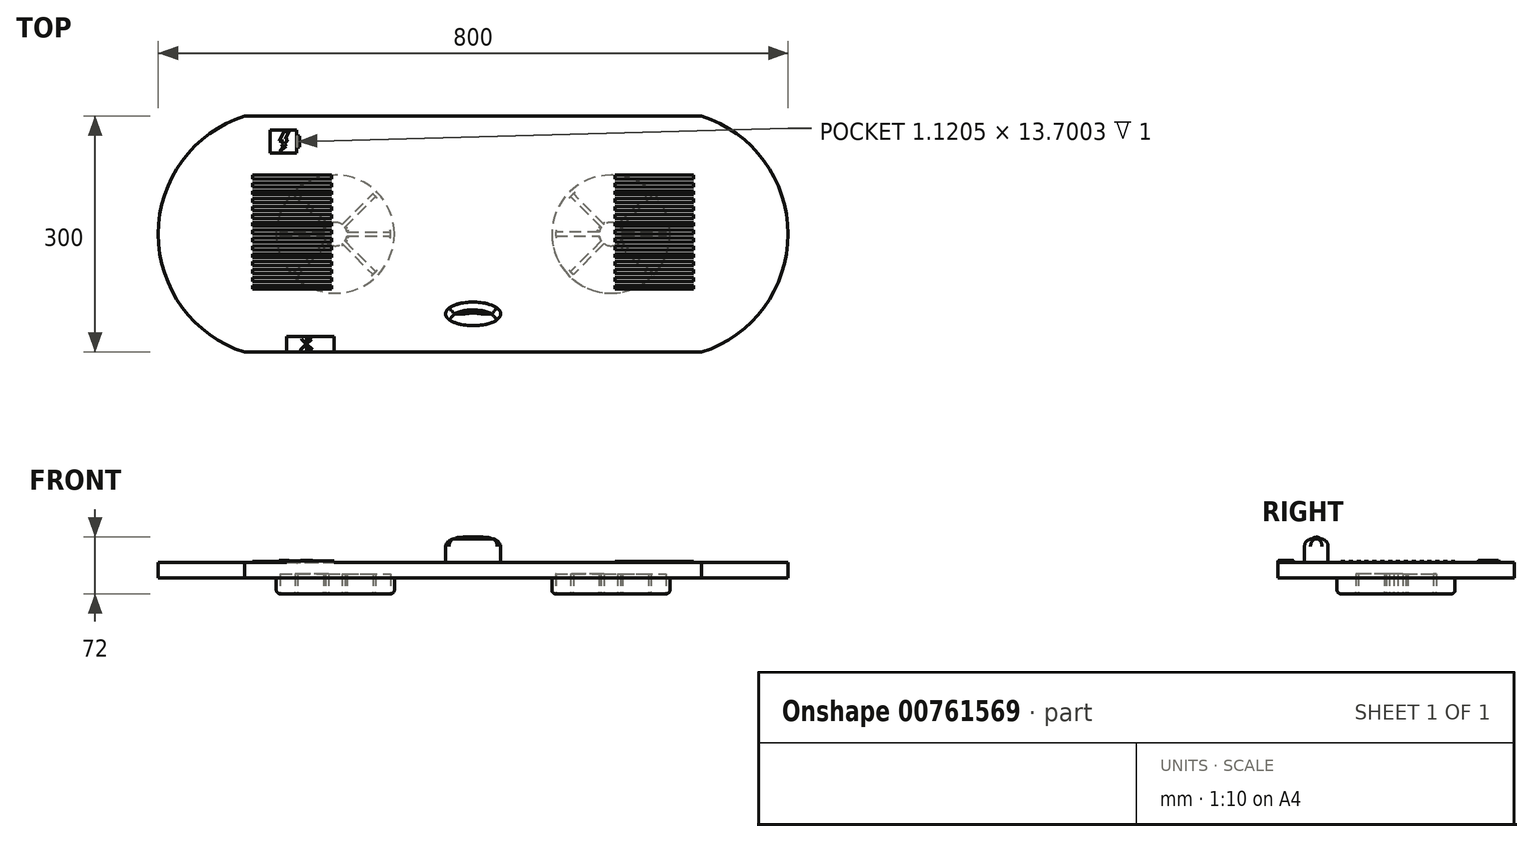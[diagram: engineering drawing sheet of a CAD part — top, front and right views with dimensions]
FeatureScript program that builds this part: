
annotation { "Feature Type Name" : "Feature", "Feature Type Description" : "" }
export const myFeature = defineFeature(function(context is Context, id is Id, definition is map)
    precondition{}
    {
        {
            var Q0;
            Q0=qCreatedBy(makeId("Top.planeOp"),FACE);
            var sketch = newSketch(context, id + "F0", { "sketchPlane" : qUnion([Q0])});
            skLineSegment(sketch, "E0.bottom", {"start": v(400, 150) * mm, "end": v(-400, 150) * mm});
            skLineSegment(sketch, "E0.top", {"start": v(400, -150) * mm, "end": v(-400, -150) * mm});
            skLineSegment(sketch, "E0.left", {"start": v(400, 150) * mm, "end": v(400, -150) * mm});
            skLineSegment(sketch, "E0.right", {"start": v(-400, 150) * mm, "end": v(-400, -150) * mm});
            skPoint(sketch, "E0.middle", {"position": v(0, 0) * mm});
            skArc(sketch, "E1", {"start": v(-290, 150) * mm, "mid": v(-400, 0) * mm, "end": v(-290, -150) * mm});
            skArc(sketch, "E2", {"start": v(290, -150) * mm, "mid": v(400, 0) * mm, "end": v(290, 150) * mm});
            skSolve(sketch);
        }
        {
            var Q0;
            {var subQ0=sQuery(id+"F0.wireOp",EDGE,"E1");var subQ1=sQuery(id+"F0.wireOp",EDGE,"E0.bottom");var subQ2=makeQuery(id+"F0.imprint","INTERSECT",VERTEX,{"derivedFrom":[subQ1,subQ0]});Q0=makeQuery(id+"F0.imprint","IMPRINT",FACE,{"disambiguationData":[TD([[makeQuery(id+"F0.imprint","IMPRINT",EDGE,{"disambiguationData":[TD([[subQ2,1.0]])],"derivedFrom":subQ1}),1.0]])]});}
            extrude(context, id + "F1", {"entities" : qUnion([Q0]), "depth" : 20 * mm, "offsetDistance" : 25 * mm});
        }
        {
            var Q0;
            Q0=makeQuery(id+"F1.opExtrude","CAP_FACE",FACE,{"disambiguationData":[OSD([sQuery(id+"F0.wireOp",EDGE,"E0.bottom"),sQuery(id+"F0.wireOp",EDGE,"E0.top"),sQuery(id+"F0.wireOp",EDGE,"E1"),sQuery(id+"F0.wireOp",EDGE,"E2")])],"isStart":true});
            var sketch = newSketch(context, id + "F2", { "sketchPlane" : qUnion([Q0])});
            skCircle(sketch, "E3", {"center": v(-175, 0) * mm, "radius": 75 * mm});
            skCircle(sketch, "E4", {"center": v(175, 0) * mm, "radius": 75 * mm});
            skSolve(sketch);
        }
        {
            var Q0;
            Q0=makeQuery(id+"F2.imprint","IMPRINT",FACE,{"disambiguationData":[TD([[makeQuery(id+"F2.imprint","IMPRINT",EDGE,{"derivedFrom":sQuery(id+"F2.wireOp",EDGE,"E3")}),1.0]])]});
            var Q1;
            Q1=makeQuery(id+"F2.imprint","IMPRINT",FACE,{"disambiguationData":[TD([[makeQuery(id+"F2.imprint","IMPRINT",EDGE,{"derivedFrom":sQuery(id+"F2.wireOp",EDGE,"E4")}),1.0]])]});
            extrude(context, id + "F3", {"entities" : qUnion([Q0, Q1]), "operationType" : NewBodyOperationType.ADD, "depth" : 20 * mm, "offsetDistance" : 25 * mm});
        }
        {
            var Q0;
            Q0=makeQuery(id+"F3.opExtrude","CAP_FACE",FACE,{"disambiguationData":[OSD([sQuery(id+"F2.wireOp",EDGE,"E3")])],"isStart":false});
            var Q1;
            Q1=makeQuery(id+"F3.opExtrude","CAP_FACE",FACE,{"disambiguationData":[OSD([sQuery(id+"F2.wireOp",EDGE,"E4")])],"isStart":false});
            fillet(context, id + "F4", {"entities" : qUnion([Q0, Q1]), "radius" : 5 * mm, "tangentPropagation" : true, "allowEdgeOverflow" : false});
        }
        {
            var Q0;
            Q0=makeQuery(id+"F1.opExtrude","CAP_FACE",FACE,{"disambiguationData":[OSD([sQuery(id+"F0.wireOp",EDGE,"E0.bottom"),sQuery(id+"F0.wireOp",EDGE,"E0.top"),sQuery(id+"F0.wireOp",EDGE,"E1"),sQuery(id+"F0.wireOp",EDGE,"E2")])],"isStart":false});
            var sketch = newSketch(context, id + "F5", { "sketchPlane" : qUnion([Q0])});
            skLineSegment(sketch, "E5.bottom", {"start": v(-236.75, -150) * mm, "end": v(-176.75, -150) * mm});
            skLineSegment(sketch, "E5.top", {"start": v(-236.75, -130) * mm, "end": v(-176.75, -130) * mm});
            skLineSegment(sketch, "E5.left", {"start": v(-236.75, -150) * mm, "end": v(-236.75, -130) * mm});
            skLineSegment(sketch, "E5.right", {"start": v(-176.75, -150) * mm, "end": v(-176.75, -130) * mm});
            skSolve(sketch);
        }
        {
            var Q0;
            Q0=makeQuery(id+"F5.imprint","IMPRINT",FACE,{"disambiguationData":[TD([[makeQuery(id+"F5.imprint","IMPRINT",EDGE,{"derivedFrom":sQuery(id+"F5.wireOp",EDGE,"E5.bottom")}),-1.0]])]});
            var sketch = newSketch(context, id + "F6", { "sketchPlane" : qUnion([Q0])});
            skLineSegment(sketch, "E6", {"start": v(-219.31, -146.88) * mm, "end": v(-218.82, -147.38) * mm});
            skLineSegment(sketch, "E7", {"start": v(-212.24, -139.81) * mm, "end": v(-218.05, -134) * mm});
            skLineSegment(sketch, "E8", {"start": v(-218.05, -134) * mm, "end": v(-217.56, -133.5) * mm});
            skLineSegment(sketch, "E9", {"start": v(-211.74, -139.32) * mm, "end": v(-211.74, -130.32) * mm});
            skLineSegment(sketch, "E10", {"start": v(-211.74, -130.32) * mm, "end": v(-205.43, -134) * mm});
            skLineSegment(sketch, "E11", {"start": v(-211.74, -140.3) * mm, "end": v(-211.74, -149.3) * mm});
            skLineSegment(sketch, "E12", {"start": v(-212.24, -139.81) * mm, "end": v(-219.31, -146.88) * mm});
            skLineSegment(sketch, "E13", {"start": v(-204.18, -146.88) * mm, "end": v(-211.74, -149.3) * mm});
            skLineSegment(sketch, "E14", {"start": v(-211.74, -140.3) * mm, "end": v(-218.82, -147.38) * mm});
            skLineSegment(sketch, "E15", {"start": v(-211.25, -139.81) * mm, "end": v(-210.45, -139.02) * mm});
            skLineSegment(sketch, "E16", {"start": v(-210.45, -139.02) * mm, "end": v(-205.43, -134) * mm});
            skLineSegment(sketch, "E17", {"start": v(-217.56, -133.5) * mm, "end": v(-211.74, -139.32) * mm});
            skLineSegment(sketch, "E18", {"start": v(-204.18, -146.88) * mm, "end": v(-211.25, -139.81) * mm});
            skLineSegment(sketch, "E19", {"start": v(-211.25, -131.3) * mm, "end": v(-211.25, -138.81) * mm});
            skLineSegment(sketch, "E20", {"start": v(-211.25, -131.3) * mm, "end": v(-207.16, -133.69) * mm});
            skLineSegment(sketch, "E21", {"start": v(-207.16, -133.69) * mm, "end": v(-206.93, -133.82) * mm});
            skLineSegment(sketch, "E22", {"start": v(-206.93, -133.82) * mm, "end": v(-211.25, -138.81) * mm});
            skLineSegment(sketch, "E23", {"start": v(-211.25, -140.95) * mm, "end": v(-211.25, -148.29) * mm});
            skLineSegment(sketch, "E24", {"start": v(-211.25, -148.29) * mm, "end": v(-206.47, -146.82) * mm});
            skLineSegment(sketch, "E25", {"start": v(-206.47, -146.82) * mm, "end": v(-211.25, -140.95) * mm});
            skSolve(sketch);
        }
        {
            var Q0;
            Q0=makeQuery(id+"F6.imprint","IMPRINT",FACE,{"disambiguationData":[TD([[makeQuery(id+"F6.imprint","IMPRINT",EDGE,{"derivedFrom":sQuery(id+"F6.wireOp",EDGE,"E6")}),1.0]])]});
            var Q1;
            Q1 = qSketchRegion(id + "F8", true);
            var Q2;
            Q2 = qSketchRegion(id + "F5", true);
            extrude(context, id + "F7", {"entities" : qUnion([Q0, Q1, Q2]), "operationType" : NewBodyOperationType.ADD, "depth" : 2 * mm, "offsetDistance" : 25 * mm});
        }
        {
            var Q0;
            Q0=makeQuery(id+"F3.opExtrude","CAP_FACE",FACE,{"disambiguationData":[OSD([sQuery(id+"F2.wireOp",EDGE,"E3")])],"isStart":false});
            var sketch = newSketch(context, id + "F8", { "sketchPlane" : qUnion([Q0])});
            skCircle(sketch, "E26", {"center": v(-175, 0) * mm, "radius": 15 * mm});
            skLineSegment(sketch, "E27", {"start": v(-177.5, 14.8) * mm, "end": v(-177.5, 70) * mm});
            skLineSegment(sketch, "E28", {"start": v(-172.5, 14.8) * mm, "end": v(-172.5, 69.96) * mm});
            skLineSegment(sketch, "E29", {"start": v(-177.5, -14.8) * mm, "end": v(-177.5, -69.96) * mm});
            skLineSegment(sketch, "E30", {"start": v(-172.5, -14.8) * mm, "end": v(-172.5, -69.96) * mm});
            skLineSegment(sketch, "E31", {"start": v(-190, 2.5) * mm, "end": v(-189.8, 2.5) * mm});
            skLineSegment(sketch, "E32", {"start": v(-190, -2.5) * mm, "end": v(-189.8, -2.5) * mm});
            skLineSegment(sketch, "E33", {"start": v(-189.8, 2.5) * mm, "end": v(-244.96, 2.5) * mm});
            skLineSegment(sketch, "E34", {"start": v(-190, -2.5) * mm, "end": v(-244.96, -2.5) * mm});
            skLineSegment(sketch, "E35.1.0", {"start": v(-183.84, -12.37) * mm, "end": v(-222.7, -51.23) * mm});
            skLineSegment(sketch, "E35.1.1", {"start": v(-183.84, -12.37) * mm, "end": v(-183.7, -12.23) * mm});
            skLineSegment(sketch, "E35.1.2", {"start": v(-187.23, -8.7) * mm, "end": v(-226.23, -47.7) * mm});
            skLineSegment(sketch, "E35.2.0", {"start": v(-172.5, -15) * mm, "end": v(-172.5, -69.96) * mm});
            skLineSegment(sketch, "E35.2.1", {"start": v(-172.5, -15) * mm, "end": v(-172.5, -14.8) * mm});
            skLineSegment(sketch, "E35.3.0", {"start": v(-162.63, -8.84) * mm, "end": v(-123.77, -47.7) * mm});
            skLineSegment(sketch, "E35.3.1", {"start": v(-162.63, -8.84) * mm, "end": v(-162.77, -8.7) * mm});
            skLineSegment(sketch, "E35.3.2", {"start": v(-166.3, -12.23) * mm, "end": v(-127.3, -51.23) * mm});
            skLineSegment(sketch, "E35.4.0", {"start": v(-160, 2.5) * mm, "end": v(-105.04, 2.5) * mm});
            skLineSegment(sketch, "E35.4.1", {"start": v(-160, 2.5) * mm, "end": v(-160.2, 2.5) * mm});
            skLineSegment(sketch, "E35.4.2", {"start": v(-160.2, -2.5) * mm, "end": v(-105.04, -2.5) * mm});
            skLineSegment(sketch, "E35.5.0", {"start": v(-166.16, 12.37) * mm, "end": v(-127.3, 51.23) * mm});
            skLineSegment(sketch, "E35.5.1", {"start": v(-166.16, 12.37) * mm, "end": v(-166.3, 12.23) * mm});
            skLineSegment(sketch, "E35.5.2", {"start": v(-162.77, 8.7) * mm, "end": v(-123.77, 47.7) * mm});
            skLineSegment(sketch, "E35.6.0", {"start": v(-177.5, 15) * mm, "end": v(-177.5, 69.96) * mm});
            skLineSegment(sketch, "E35.6.1", {"start": v(-177.5, 15) * mm, "end": v(-177.5, 14.8) * mm});
            skLineSegment(sketch, "E35.7.0", {"start": v(-187.37, 8.84) * mm, "end": v(-226.23, 47.7) * mm});
            skLineSegment(sketch, "E35.7.1", {"start": v(-187.37, 8.84) * mm, "end": v(-187.23, 8.7) * mm});
            skLineSegment(sketch, "E35.7.2", {"start": v(-183.7, 12.23) * mm, "end": v(-222.7, 51.23) * mm});
            skSolve(sketch);
        }
        {
            var Q0;
            Q0 = qSketchRegion(id + "F6", true);
            extrude(context, id + "F9", {"entities" : qUnion([Q0]), "operationType" : NewBodyOperationType.ADD, "depth" : 2.5 * mm, "offsetDistance" : 25 * mm});
        }
        {
            var Q0;
            Q0=makeQuery(id+"F3.opExtrude","CAP_FACE",FACE,{"disambiguationData":[OSD([sQuery(id+"F2.wireOp",EDGE,"E4")])],"isStart":false});
            var sketch = newSketch(context, id + "F10", { "sketchPlane" : qUnion([Q0])});
            skPoint(sketch, "E36", {"position": v(175, 0) * mm});
            skCircle(sketch, "E37", {"center": v(175, 0) * mm, "radius": 15 * mm});
            skLineSegment(sketch, "E38", {"start": v(172.5, 14.8) * mm, "end": v(172.5, 70) * mm});
            skLineSegment(sketch, "E39", {"start": v(177.5, 14.8) * mm, "end": v(177.5, 69.96) * mm});
            skLineSegment(sketch, "E40", {"start": v(172.5, -14.8) * mm, "end": v(172.5, -69.96) * mm});
            skLineSegment(sketch, "E41", {"start": v(177.5, -14.8) * mm, "end": v(177.5, -69.96) * mm});
            skLineSegment(sketch, "E42", {"start": v(160, 2.5) * mm, "end": v(160.2, 2.5) * mm});
            skLineSegment(sketch, "E43", {"start": v(160, -2.5) * mm, "end": v(160.2, -2.5) * mm});
            skLineSegment(sketch, "E44", {"start": v(160.2, 2.5) * mm, "end": v(105.04, 2.5) * mm});
            skLineSegment(sketch, "E45", {"start": v(160, -2.5) * mm, "end": v(105.04, -2.5) * mm});
            skLineSegment(sketch, "E46.1.0", {"start": v(166.16, -12.37) * mm, "end": v(127.3, -51.23) * mm});
            skLineSegment(sketch, "E46.1.1", {"start": v(166.16, -12.37) * mm, "end": v(166.3, -12.23) * mm});
            skLineSegment(sketch, "E46.1.2", {"start": v(162.77, -8.7) * mm, "end": v(123.77, -47.7) * mm});
            skLineSegment(sketch, "E46.2.0", {"start": v(177.5, -15) * mm, "end": v(177.5, -69.96) * mm});
            skLineSegment(sketch, "E46.2.1", {"start": v(177.5, -15) * mm, "end": v(177.5, -14.8) * mm});
            skLineSegment(sketch, "E46.3.0", {"start": v(187.37, -8.84) * mm, "end": v(226.23, -47.7) * mm});
            skLineSegment(sketch, "E46.3.1", {"start": v(187.37, -8.84) * mm, "end": v(187.23, -8.7) * mm});
            skLineSegment(sketch, "E46.3.2", {"start": v(183.7, -12.23) * mm, "end": v(222.7, -51.23) * mm});
            skLineSegment(sketch, "E46.4.0", {"start": v(190, 2.5) * mm, "end": v(244.96, 2.5) * mm});
            skLineSegment(sketch, "E46.4.1", {"start": v(190, 2.5) * mm, "end": v(189.8, 2.5) * mm});
            skLineSegment(sketch, "E46.4.2", {"start": v(189.8, -2.5) * mm, "end": v(244.96, -2.5) * mm});
            skLineSegment(sketch, "E46.5.0", {"start": v(183.84, 12.37) * mm, "end": v(222.7, 51.23) * mm});
            skLineSegment(sketch, "E46.5.1", {"start": v(183.84, 12.37) * mm, "end": v(183.7, 12.23) * mm});
            skLineSegment(sketch, "E46.5.2", {"start": v(187.23, 8.7) * mm, "end": v(226.23, 47.7) * mm});
            skLineSegment(sketch, "E46.6.0", {"start": v(172.5, 15) * mm, "end": v(172.5, 69.96) * mm});
            skLineSegment(sketch, "E46.6.1", {"start": v(172.5, 15) * mm, "end": v(172.5, 14.8) * mm});
            skLineSegment(sketch, "E46.7.0", {"start": v(162.63, 8.84) * mm, "end": v(123.77, 47.7) * mm});
            skLineSegment(sketch, "E46.7.1", {"start": v(162.63, 8.84) * mm, "end": v(162.77, 8.7) * mm});
            skLineSegment(sketch, "E46.7.2", {"start": v(166.3, 12.23) * mm, "end": v(127.3, 51.23) * mm});
            skSolve(sketch);
        }
        {
            var Q0;
            {var subQ0=sQuery(id+"F8.wireOp",EDGE,"E26");var subQ8=makeQuery(id+"F8.imprint","INTERSECT",VERTEX,{"derivedFrom":[subQ0,sQuery(id+"F8.wireOp",EDGE,"E35.4.1")]});Q0=makeQuery(id+"F8.imprint","IMPRINT",FACE,{"disambiguationData":[TD([[makeQuery(id+"F8.imprint","IMPRINT",EDGE,{"disambiguationData":[TD([[subQ8,-1.0]])],"derivedFrom":subQ0}),1.0]])]});}
            var Q1;
            {var subQ1=sQuery(id+"F8.wireOp",EDGE,"E35.7.0");Q1=makeQuery(id+"F8.imprint","IMPRINT",FACE,{"disambiguationData":[TD([[makeQuery(id+"F8.imprint","IMPRINT",EDGE,{"derivedFrom":subQ1}),-1.0]])]});}
            var Q2;
            {var subQ5=sQuery(id+"F8.wireOp",EDGE,"E32");Q2=makeQuery(id+"F8.imprint","IMPRINT",FACE,{"disambiguationData":[TD([[makeQuery(id+"F8.imprint","IMPRINT",EDGE,{"derivedFrom":subQ5}),1.0]])]});}
            var Q3;
            {var subQ2=sQuery(id+"F8.wireOp",EDGE,"E35.1.0");Q3=makeQuery(id+"F8.imprint","IMPRINT",FACE,{"disambiguationData":[TD([[makeQuery(id+"F8.imprint","IMPRINT",EDGE,{"derivedFrom":subQ2}),-1.0]])]});}
            var Q4;
            {var subQ2=sQuery(id+"F8.wireOp",EDGE,"E35.2.0");Q4=makeQuery(id+"F8.imprint","IMPRINT",FACE,{"disambiguationData":[TD([[makeQuery(id+"F8.imprint","IMPRINT",EDGE,{"derivedFrom":subQ2}),-1.0]])]});}
            var Q5;
            {var subQ1=sQuery(id+"F8.wireOp",EDGE,"E35.3.0");Q5=makeQuery(id+"F8.imprint","IMPRINT",FACE,{"disambiguationData":[TD([[makeQuery(id+"F8.imprint","IMPRINT",EDGE,{"derivedFrom":subQ1}),-1.0]])]});}
            var Q6;
            {var subQ1=sQuery(id+"F8.wireOp",EDGE,"E35.4.0");Q6=makeQuery(id+"F8.imprint","IMPRINT",FACE,{"disambiguationData":[TD([[makeQuery(id+"F8.imprint","IMPRINT",EDGE,{"derivedFrom":subQ1}),-1.0]])]});}
            var Q7;
            {var subQ3=sQuery(id+"F8.wireOp",EDGE,"E35.5.0");Q7=makeQuery(id+"F8.imprint","IMPRINT",FACE,{"disambiguationData":[TD([[makeQuery(id+"F8.imprint","IMPRINT",EDGE,{"derivedFrom":subQ3}),-1.0]])]});}
            var Q8;
            {var subQ3=sQuery(id+"F8.wireOp",EDGE,"E35.6.0");Q8=makeQuery(id+"F8.imprint","IMPRINT",FACE,{"disambiguationData":[TD([[makeQuery(id+"F8.imprint","IMPRINT",EDGE,{"derivedFrom":subQ3}),-1.0]])]});}
            extrude(context, id + "F11", {"entities" : qUnion([Q0, Q1, Q2, Q3, Q4, Q5, Q6, Q7, Q8]), "operationType" : NewBodyOperationType.REMOVE, "oppositeDirection" : true, "depth" : 25 * mm, "offsetDistance" : 25 * mm});
        }
        {
            var Q0;
            Q0=makeQuery(id+"F11.boolean.opBoolean","COPY",EDGE,{"derivedFrom":makeQuery(id+"F11.opExtrude","CAP_EDGE",EDGE,{"disambiguationData":[OSD([sQuery(id+"F8.wireOp",EDGE,"E35.7.2")])],"isStart":true})});
            var Q1;
            Q1=makeQuery(id+"F11.boolean.opBoolean","COPY",EDGE,{"derivedFrom":makeQuery(id+"F11.opExtrude","CAP_EDGE",EDGE,{"disambiguationData":[OSD([sQuery(id+"F8.wireOp",EDGE,"E35.7.0"),sQuery(id+"F8.wireOp",EDGE,"E35.7.1")])],"isStart":true})});
            var Q2;
            Q2=makeQuery(id+"F11.boolean.opBoolean","COPY",EDGE,{"derivedFrom":makeQuery(id+"F11.opExtrude","CAP_EDGE",EDGE,{"disambiguationData":[OSD([sQuery(id+"F8.wireOp",EDGE,"E33")])],"isStart":true})});
            var Q3;
            Q3=makeQuery(id+"F11.boolean.opBoolean","COPY",EDGE,{"derivedFrom":makeQuery(id+"F11.opExtrude","CAP_EDGE",EDGE,{"disambiguationData":[OSD([sQuery(id+"F8.wireOp",EDGE,"E32"),sQuery(id+"F8.wireOp",EDGE,"E34")])],"isStart":true})});
            var Q4;
            Q4=makeQuery(id+"F11.boolean.opBoolean","COPY",EDGE,{"derivedFrom":makeQuery(id+"F11.opExtrude","CAP_EDGE",EDGE,{"disambiguationData":[OSD([sQuery(id+"F8.wireOp",EDGE,"E35.1.2")])],"isStart":true})});
            var Q5;
            {var subQ0=sQuery(id+"F8.wireOp",EDGE,"E26");Q5=makeQuery(id+"F11.boolean.opBoolean","COPY",EDGE,{"derivedFrom":makeQuery(id+"F11.opExtrude","CAP_EDGE",EDGE,{"disambiguationData":[OSD([subQ0]),TDD([makeQuery(id+"F8.imprint","IMPRINT",EDGE,{"disambiguationData":[TD([[makeQuery(id+"F8.imprint","INTERSECT",VERTEX,{"derivedFrom":[subQ0,sQuery(id+"F8.wireOp",EDGE,"E33")]}),1.0]])],"derivedFrom":subQ0})])],"isStart":true})});}
            var Q6;
            {var subQ0=sQuery(id+"F8.wireOp",EDGE,"E26");Q6=makeQuery(id+"F11.boolean.opBoolean","COPY",EDGE,{"derivedFrom":makeQuery(id+"F11.opExtrude","CAP_EDGE",EDGE,{"disambiguationData":[OSD([subQ0]),TDD([makeQuery(id+"F8.imprint","IMPRINT",EDGE,{"disambiguationData":[TD([[makeQuery(id+"F8.imprint","INTERSECT",VERTEX,{"derivedFrom":[subQ0,sQuery(id+"F8.wireOp",EDGE,"E32")]}),-1.0]])],"derivedFrom":subQ0})])],"isStart":true})});}
            var Q7;
            Q7=makeQuery(id+"F11.boolean.opBoolean","COPY",EDGE,{"derivedFrom":makeQuery(id+"F11.opExtrude","CAP_EDGE",EDGE,{"disambiguationData":[OSD([sQuery(id+"F8.wireOp",EDGE,"E35.1.0"),sQuery(id+"F8.wireOp",EDGE,"E35.1.1")])],"isStart":true})});
            var Q8;
            {var subQ0=sQuery(id+"F8.wireOp",EDGE,"E26");Q8=makeQuery(id+"F11.boolean.opBoolean","COPY",EDGE,{"derivedFrom":makeQuery(id+"F11.opExtrude","CAP_EDGE",EDGE,{"disambiguationData":[OSD([subQ0]),TDD([makeQuery(id+"F8.imprint","IMPRINT",EDGE,{"disambiguationData":[TD([[makeQuery(id+"F8.imprint","INTERSECT",VERTEX,{"derivedFrom":[subQ0,sQuery(id+"F8.wireOp",EDGE,"E35.1.1")]}),-1.0]])],"derivedFrom":subQ0})])],"isStart":true})});}
            var Q9;
            Q9=makeQuery(id+"F11.boolean.opBoolean","COPY",EDGE,{"derivedFrom":makeQuery(id+"F11.opExtrude","CAP_EDGE",EDGE,{"disambiguationData":[OSD([sQuery(id+"F8.wireOp",EDGE,"E29")])],"isStart":true})});
            var Q10;
            Q10=makeQuery(id+"F11.boolean.opBoolean","COPY",EDGE,{"derivedFrom":makeQuery(id+"F11.opExtrude","CAP_EDGE",EDGE,{"disambiguationData":[OSD([sQuery(id+"F8.wireOp",EDGE,"E35.2.0"),sQuery(id+"F8.wireOp",EDGE,"E35.2.1")])],"isStart":true})});
            var Q11;
            {var subQ0=sQuery(id+"F8.wireOp",EDGE,"E26");Q11=makeQuery(id+"F11.boolean.opBoolean","COPY",EDGE,{"derivedFrom":makeQuery(id+"F11.opExtrude","CAP_EDGE",EDGE,{"disambiguationData":[OSD([subQ0]),TDD([makeQuery(id+"F8.imprint","IMPRINT",EDGE,{"disambiguationData":[TD([[makeQuery(id+"F8.imprint","INTERSECT",VERTEX,{"derivedFrom":[subQ0,sQuery(id+"F8.wireOp",EDGE,"E35.2.1")]}),-1.0]])],"derivedFrom":subQ0})])],"isStart":true})});}
            var Q12;
            Q12=makeQuery(id+"F11.boolean.opBoolean","COPY",EDGE,{"derivedFrom":makeQuery(id+"F11.opExtrude","CAP_EDGE",EDGE,{"disambiguationData":[OSD([sQuery(id+"F8.wireOp",EDGE,"E35.3.2")])],"isStart":true})});
            var Q13;
            Q13=makeQuery(id+"F11.boolean.opBoolean","COPY",EDGE,{"derivedFrom":makeQuery(id+"F11.opExtrude","CAP_EDGE",EDGE,{"disambiguationData":[OSD([sQuery(id+"F8.wireOp",EDGE,"E35.3.0"),sQuery(id+"F8.wireOp",EDGE,"E35.3.1")])],"isStart":true})});
            var Q14;
            {var subQ0=sQuery(id+"F8.wireOp",EDGE,"E26");Q14=makeQuery(id+"F11.boolean.opBoolean","COPY",EDGE,{"derivedFrom":makeQuery(id+"F11.opExtrude","CAP_EDGE",EDGE,{"disambiguationData":[OSD([subQ0]),TDD([makeQuery(id+"F8.imprint","IMPRINT",EDGE,{"disambiguationData":[TD([[makeQuery(id+"F8.imprint","INTERSECT",VERTEX,{"derivedFrom":[subQ0,sQuery(id+"F8.wireOp",EDGE,"E35.3.1")]}),-1.0]])],"derivedFrom":subQ0})])],"isStart":true})});}
            var Q15;
            Q15=makeQuery(id+"F11.boolean.opBoolean","COPY",EDGE,{"derivedFrom":makeQuery(id+"F11.opExtrude","CAP_EDGE",EDGE,{"disambiguationData":[OSD([sQuery(id+"F8.wireOp",EDGE,"E35.4.2")])],"isStart":true})});
            var Q16;
            Q16=makeQuery(id+"F11.boolean.opBoolean","COPY",EDGE,{"derivedFrom":makeQuery(id+"F11.opExtrude","CAP_EDGE",EDGE,{"disambiguationData":[OSD([sQuery(id+"F8.wireOp",EDGE,"E35.4.0"),sQuery(id+"F8.wireOp",EDGE,"E35.4.1")])],"isStart":true})});
            var Q17;
            {var subQ0=sQuery(id+"F8.wireOp",EDGE,"E26");Q17=makeQuery(id+"F11.boolean.opBoolean","COPY",EDGE,{"derivedFrom":makeQuery(id+"F11.opExtrude","CAP_EDGE",EDGE,{"disambiguationData":[OSD([subQ0]),TDD([makeQuery(id+"F8.imprint","IMPRINT",EDGE,{"disambiguationData":[TD([[makeQuery(id+"F8.imprint","INTERSECT",VERTEX,{"derivedFrom":[subQ0,sQuery(id+"F8.wireOp",EDGE,"E35.4.1")]}),-1.0]])],"derivedFrom":subQ0})])],"isStart":true})});}
            var Q18;
            Q18=makeQuery(id+"F11.boolean.opBoolean","COPY",EDGE,{"derivedFrom":makeQuery(id+"F11.opExtrude","CAP_EDGE",EDGE,{"disambiguationData":[OSD([sQuery(id+"F8.wireOp",EDGE,"E35.5.2")])],"isStart":true})});
            var Q19;
            Q19=makeQuery(id+"F11.boolean.opBoolean","COPY",EDGE,{"derivedFrom":makeQuery(id+"F11.opExtrude","CAP_EDGE",EDGE,{"disambiguationData":[OSD([sQuery(id+"F8.wireOp",EDGE,"E35.5.0"),sQuery(id+"F8.wireOp",EDGE,"E35.5.1")])],"isStart":true})});
            var Q20;
            {var subQ0=sQuery(id+"F8.wireOp",EDGE,"E26");Q20=makeQuery(id+"F11.boolean.opBoolean","COPY",EDGE,{"derivedFrom":makeQuery(id+"F11.opExtrude","CAP_EDGE",EDGE,{"disambiguationData":[OSD([subQ0]),TDD([makeQuery(id+"F8.imprint","IMPRINT",EDGE,{"disambiguationData":[TD([[makeQuery(id+"F8.imprint","INTERSECT",VERTEX,{"derivedFrom":[subQ0,sQuery(id+"F8.wireOp",EDGE,"E35.5.1")]}),-1.0]])],"derivedFrom":subQ0})])],"isStart":true})});}
            var Q21;
            Q21=makeQuery(id+"F11.boolean.opBoolean","COPY",EDGE,{"derivedFrom":makeQuery(id+"F11.opExtrude","CAP_EDGE",EDGE,{"disambiguationData":[OSD([sQuery(id+"F8.wireOp",EDGE,"E28")])],"isStart":true})});
            var Q22;
            Q22=makeQuery(id+"F11.boolean.opBoolean","COPY",EDGE,{"derivedFrom":makeQuery(id+"F11.opExtrude","CAP_EDGE",EDGE,{"disambiguationData":[OSD([sQuery(id+"F8.wireOp",EDGE,"E35.6.0"),sQuery(id+"F8.wireOp",EDGE,"E35.6.1")])],"isStart":true})});
            var Q23;
            {var subQ0=sQuery(id+"F8.wireOp",EDGE,"E26");Q23=makeQuery(id+"F11.boolean.opBoolean","COPY",EDGE,{"derivedFrom":makeQuery(id+"F11.opExtrude","CAP_EDGE",EDGE,{"disambiguationData":[OSD([subQ0]),TDD([makeQuery(id+"F8.imprint","IMPRINT",EDGE,{"disambiguationData":[TD([[makeQuery(id+"F8.imprint","INTERSECT",VERTEX,{"derivedFrom":[subQ0,sQuery(id+"F8.wireOp",EDGE,"E35.6.1")]}),-1.0]])],"derivedFrom":subQ0})])],"isStart":true})});}
            fillet(context, id + "F12", {"entities" : qUnion([Q0, Q1, Q2, Q3, Q4, Q5, Q6, Q7, Q8, Q9, Q10, Q11, Q12, Q13, Q14, Q15, Q16, Q17, Q18, Q19, Q20, Q21, Q22, Q23]), "radius" : 2.5 * mm, "tangentPropagation" : true, "allowEdgeOverflow" : false});
        }
        {
            var Q0;
            {var subQ3=sQuery(id+"F10.wireOp",EDGE,"E46.6.0");Q0=makeQuery(id+"F10.imprint","IMPRINT",FACE,{"disambiguationData":[TD([[makeQuery(id+"F10.imprint","IMPRINT",EDGE,{"derivedFrom":subQ3}),-1.0]])]});}
            var Q1;
            {var subQ1=sQuery(id+"F10.wireOp",EDGE,"E46.7.0");Q1=makeQuery(id+"F10.imprint","IMPRINT",FACE,{"disambiguationData":[TD([[makeQuery(id+"F10.imprint","IMPRINT",EDGE,{"derivedFrom":subQ1}),-1.0]])]});}
            var Q2;
            {var subQ5=sQuery(id+"F10.wireOp",EDGE,"E43");Q2=makeQuery(id+"F10.imprint","IMPRINT",FACE,{"disambiguationData":[TD([[makeQuery(id+"F10.imprint","IMPRINT",EDGE,{"derivedFrom":subQ5}),1.0]])]});}
            var Q3;
            {var subQ2=sQuery(id+"F10.wireOp",EDGE,"E46.1.0");Q3=makeQuery(id+"F10.imprint","IMPRINT",FACE,{"disambiguationData":[TD([[makeQuery(id+"F10.imprint","IMPRINT",EDGE,{"derivedFrom":subQ2}),-1.0]])]});}
            var Q4;
            {var subQ2=sQuery(id+"F10.wireOp",EDGE,"E46.2.0");Q4=makeQuery(id+"F10.imprint","IMPRINT",FACE,{"disambiguationData":[TD([[makeQuery(id+"F10.imprint","IMPRINT",EDGE,{"derivedFrom":subQ2}),-1.0]])]});}
            var Q5;
            {var subQ1=sQuery(id+"F10.wireOp",EDGE,"E46.3.0");Q5=makeQuery(id+"F10.imprint","IMPRINT",FACE,{"disambiguationData":[TD([[makeQuery(id+"F10.imprint","IMPRINT",EDGE,{"derivedFrom":subQ1}),-1.0]])]});}
            var Q6;
            {var subQ1=sQuery(id+"F10.wireOp",EDGE,"E46.4.0");Q6=makeQuery(id+"F10.imprint","IMPRINT",FACE,{"disambiguationData":[TD([[makeQuery(id+"F10.imprint","IMPRINT",EDGE,{"derivedFrom":subQ1}),-1.0]])]});}
            var Q7;
            {var subQ3=sQuery(id+"F10.wireOp",EDGE,"E46.5.0");Q7=makeQuery(id+"F10.imprint","IMPRINT",FACE,{"disambiguationData":[TD([[makeQuery(id+"F10.imprint","IMPRINT",EDGE,{"derivedFrom":subQ3}),-1.0]])]});}
            var Q8;
            {var subQ0=sQuery(id+"F10.wireOp",EDGE,"E37");var subQ8=makeQuery(id+"F10.imprint","INTERSECT",VERTEX,{"derivedFrom":[subQ0,sQuery(id+"F10.wireOp",EDGE,"E46.4.1")]});Q8=makeQuery(id+"F10.imprint","IMPRINT",FACE,{"disambiguationData":[TD([[makeQuery(id+"F10.imprint","IMPRINT",EDGE,{"disambiguationData":[TD([[subQ8,-1.0]])],"derivedFrom":subQ0}),1.0]])]});}
            extrude(context, id + "F13", {"entities" : qUnion([Q0, Q1, Q2, Q3, Q4, Q5, Q6, Q7, Q8]), "operationType" : NewBodyOperationType.REMOVE, "oppositeDirection" : true, "depth" : 25 * mm, "offsetDistance" : 25 * mm});
        }
        {
            var Q0;
            Q0=makeQuery(id+"F13.boolean.opBoolean","COPY",EDGE,{"derivedFrom":makeQuery(id+"F13.opExtrude","CAP_EDGE",EDGE,{"disambiguationData":[OSD([sQuery(id+"F10.wireOp",EDGE,"E46.7.0"),sQuery(id+"F10.wireOp",EDGE,"E46.7.1")])],"isStart":true})});
            var Q1;
            Q1=makeQuery(id+"F13.boolean.opBoolean","COPY",EDGE,{"derivedFrom":makeQuery(id+"F13.opExtrude","CAP_EDGE",EDGE,{"disambiguationData":[OSD([sQuery(id+"F10.wireOp",EDGE,"E46.7.2")])],"isStart":true})});
            var Q2;
            {var subQ0=sQuery(id+"F10.wireOp",EDGE,"E37");Q2=makeQuery(id+"F13.boolean.opBoolean","COPY",EDGE,{"derivedFrom":makeQuery(id+"F13.opExtrude","CAP_EDGE",EDGE,{"disambiguationData":[OSD([subQ0]),TDD([makeQuery(id+"F10.imprint","IMPRINT",EDGE,{"disambiguationData":[TD([[makeQuery(id+"F10.imprint","INTERSECT",VERTEX,{"derivedFrom":[subQ0,sQuery(id+"F10.wireOp",EDGE,"E44")]}),1.0]])],"derivedFrom":subQ0})])],"isStart":true})});}
            var Q3;
            Q3=makeQuery(id+"F13.boolean.opBoolean","COPY",EDGE,{"derivedFrom":makeQuery(id+"F13.opExtrude","CAP_EDGE",EDGE,{"disambiguationData":[OSD([sQuery(id+"F10.wireOp",EDGE,"E44")])],"isStart":true})});
            var Q4;
            Q4=makeQuery(id+"F13.boolean.opBoolean","COPY",EDGE,{"derivedFrom":makeQuery(id+"F13.opExtrude","CAP_EDGE",EDGE,{"disambiguationData":[OSD([sQuery(id+"F10.wireOp",EDGE,"E43"),sQuery(id+"F10.wireOp",EDGE,"E45")])],"isStart":true})});
            var Q5;
            {var subQ0=sQuery(id+"F10.wireOp",EDGE,"E37");Q5=makeQuery(id+"F13.boolean.opBoolean","COPY",EDGE,{"derivedFrom":makeQuery(id+"F13.opExtrude","CAP_EDGE",EDGE,{"disambiguationData":[OSD([subQ0]),TDD([makeQuery(id+"F10.imprint","IMPRINT",EDGE,{"disambiguationData":[TD([[makeQuery(id+"F10.imprint","INTERSECT",VERTEX,{"derivedFrom":[subQ0,sQuery(id+"F10.wireOp",EDGE,"E43")]}),-1.0]])],"derivedFrom":subQ0})])],"isStart":true})});}
            var Q6;
            Q6=makeQuery(id+"F13.boolean.opBoolean","COPY",EDGE,{"derivedFrom":makeQuery(id+"F13.opExtrude","CAP_EDGE",EDGE,{"disambiguationData":[OSD([sQuery(id+"F10.wireOp",EDGE,"E46.1.2")])],"isStart":true})});
            var Q7;
            Q7=makeQuery(id+"F13.boolean.opBoolean","COPY",EDGE,{"derivedFrom":makeQuery(id+"F13.opExtrude","CAP_EDGE",EDGE,{"disambiguationData":[OSD([sQuery(id+"F10.wireOp",EDGE,"E46.1.0"),sQuery(id+"F10.wireOp",EDGE,"E46.1.1")])],"isStart":true})});
            var Q8;
            {var subQ0=sQuery(id+"F10.wireOp",EDGE,"E37");Q8=makeQuery(id+"F13.boolean.opBoolean","COPY",EDGE,{"derivedFrom":makeQuery(id+"F13.opExtrude","CAP_EDGE",EDGE,{"disambiguationData":[OSD([subQ0]),TDD([makeQuery(id+"F10.imprint","IMPRINT",EDGE,{"disambiguationData":[TD([[makeQuery(id+"F10.imprint","INTERSECT",VERTEX,{"derivedFrom":[subQ0,sQuery(id+"F10.wireOp",EDGE,"E46.1.1")]}),-1.0]])],"derivedFrom":subQ0})])],"isStart":true})});}
            var Q9;
            Q9=makeQuery(id+"F13.boolean.opBoolean","COPY",EDGE,{"derivedFrom":makeQuery(id+"F13.opExtrude","CAP_EDGE",EDGE,{"disambiguationData":[OSD([sQuery(id+"F10.wireOp",EDGE,"E40")])],"isStart":true})});
            var Q10;
            Q10=makeQuery(id+"F13.boolean.opBoolean","COPY",EDGE,{"derivedFrom":makeQuery(id+"F13.opExtrude","CAP_EDGE",EDGE,{"disambiguationData":[OSD([sQuery(id+"F10.wireOp",EDGE,"E46.2.0"),sQuery(id+"F10.wireOp",EDGE,"E46.2.1")])],"isStart":true})});
            var Q11;
            {var subQ0=sQuery(id+"F10.wireOp",EDGE,"E37");Q11=makeQuery(id+"F13.boolean.opBoolean","COPY",EDGE,{"derivedFrom":makeQuery(id+"F13.opExtrude","CAP_EDGE",EDGE,{"disambiguationData":[OSD([subQ0]),TDD([makeQuery(id+"F10.imprint","IMPRINT",EDGE,{"disambiguationData":[TD([[makeQuery(id+"F10.imprint","INTERSECT",VERTEX,{"derivedFrom":[subQ0,sQuery(id+"F10.wireOp",EDGE,"E46.2.1")]}),-1.0]])],"derivedFrom":subQ0})])],"isStart":true})});}
            var Q12;
            Q12=makeQuery(id+"F13.boolean.opBoolean","COPY",EDGE,{"derivedFrom":makeQuery(id+"F13.opExtrude","CAP_EDGE",EDGE,{"disambiguationData":[OSD([sQuery(id+"F10.wireOp",EDGE,"E46.3.2")])],"isStart":true})});
            var Q13;
            Q13=makeQuery(id+"F13.boolean.opBoolean","COPY",EDGE,{"derivedFrom":makeQuery(id+"F13.opExtrude","CAP_EDGE",EDGE,{"disambiguationData":[OSD([sQuery(id+"F10.wireOp",EDGE,"E46.3.0"),sQuery(id+"F10.wireOp",EDGE,"E46.3.1")])],"isStart":true})});
            var Q14;
            {var subQ0=sQuery(id+"F10.wireOp",EDGE,"E37");Q14=makeQuery(id+"F13.boolean.opBoolean","COPY",EDGE,{"derivedFrom":makeQuery(id+"F13.opExtrude","CAP_EDGE",EDGE,{"disambiguationData":[OSD([subQ0]),TDD([makeQuery(id+"F10.imprint","IMPRINT",EDGE,{"disambiguationData":[TD([[makeQuery(id+"F10.imprint","INTERSECT",VERTEX,{"derivedFrom":[subQ0,sQuery(id+"F10.wireOp",EDGE,"E46.3.1")]}),-1.0]])],"derivedFrom":subQ0})])],"isStart":true})});}
            var Q15;
            Q15=makeQuery(id+"F13.boolean.opBoolean","COPY",EDGE,{"derivedFrom":makeQuery(id+"F13.opExtrude","CAP_EDGE",EDGE,{"disambiguationData":[OSD([sQuery(id+"F10.wireOp",EDGE,"E46.4.2")])],"isStart":true})});
            var Q16;
            Q16=makeQuery(id+"F13.boolean.opBoolean","COPY",EDGE,{"derivedFrom":makeQuery(id+"F13.opExtrude","CAP_EDGE",EDGE,{"disambiguationData":[OSD([sQuery(id+"F10.wireOp",EDGE,"E46.4.0"),sQuery(id+"F10.wireOp",EDGE,"E46.4.1")])],"isStart":true})});
            var Q17;
            {var subQ0=sQuery(id+"F10.wireOp",EDGE,"E37");Q17=makeQuery(id+"F13.boolean.opBoolean","COPY",EDGE,{"derivedFrom":makeQuery(id+"F13.opExtrude","CAP_EDGE",EDGE,{"disambiguationData":[OSD([subQ0]),TDD([makeQuery(id+"F10.imprint","IMPRINT",EDGE,{"disambiguationData":[TD([[makeQuery(id+"F10.imprint","INTERSECT",VERTEX,{"derivedFrom":[subQ0,sQuery(id+"F10.wireOp",EDGE,"E46.4.1")]}),-1.0]])],"derivedFrom":subQ0})])],"isStart":true})});}
            var Q18;
            Q18=makeQuery(id+"F13.boolean.opBoolean","COPY",EDGE,{"derivedFrom":makeQuery(id+"F13.opExtrude","CAP_EDGE",EDGE,{"disambiguationData":[OSD([sQuery(id+"F10.wireOp",EDGE,"E46.5.2")])],"isStart":true})});
            var Q19;
            Q19=makeQuery(id+"F13.boolean.opBoolean","COPY",EDGE,{"derivedFrom":makeQuery(id+"F13.opExtrude","CAP_EDGE",EDGE,{"disambiguationData":[OSD([sQuery(id+"F10.wireOp",EDGE,"E46.5.0"),sQuery(id+"F10.wireOp",EDGE,"E46.5.1")])],"isStart":true})});
            var Q20;
            {var subQ0=sQuery(id+"F10.wireOp",EDGE,"E37");Q20=makeQuery(id+"F13.boolean.opBoolean","COPY",EDGE,{"derivedFrom":makeQuery(id+"F13.opExtrude","CAP_EDGE",EDGE,{"disambiguationData":[OSD([subQ0]),TDD([makeQuery(id+"F10.imprint","IMPRINT",EDGE,{"disambiguationData":[TD([[makeQuery(id+"F10.imprint","INTERSECT",VERTEX,{"derivedFrom":[subQ0,sQuery(id+"F10.wireOp",EDGE,"E46.5.1")]}),-1.0]])],"derivedFrom":subQ0})])],"isStart":true})});}
            var Q21;
            Q21=makeQuery(id+"F13.boolean.opBoolean","COPY",EDGE,{"derivedFrom":makeQuery(id+"F13.opExtrude","CAP_EDGE",EDGE,{"disambiguationData":[OSD([sQuery(id+"F10.wireOp",EDGE,"E39")])],"isStart":true})});
            var Q22;
            Q22=makeQuery(id+"F13.boolean.opBoolean","COPY",EDGE,{"derivedFrom":makeQuery(id+"F13.opExtrude","CAP_EDGE",EDGE,{"disambiguationData":[OSD([sQuery(id+"F10.wireOp",EDGE,"E46.6.0"),sQuery(id+"F10.wireOp",EDGE,"E46.6.1")])],"isStart":true})});
            var Q23;
            {var subQ0=sQuery(id+"F10.wireOp",EDGE,"E37");Q23=makeQuery(id+"F13.boolean.opBoolean","COPY",EDGE,{"derivedFrom":makeQuery(id+"F13.opExtrude","CAP_EDGE",EDGE,{"disambiguationData":[OSD([subQ0]),TDD([makeQuery(id+"F10.imprint","IMPRINT",EDGE,{"disambiguationData":[TD([[makeQuery(id+"F10.imprint","INTERSECT",VERTEX,{"derivedFrom":[subQ0,sQuery(id+"F10.wireOp",EDGE,"E46.6.1")]}),-1.0]])],"derivedFrom":subQ0})])],"isStart":true})});}
            fillet(context, id + "F14", {"entities" : qUnion([Q0, Q1, Q2, Q3, Q4, Q5, Q6, Q7, Q8, Q9, Q10, Q11, Q12, Q13, Q14, Q15, Q16, Q17, Q18, Q19, Q20, Q21, Q22, Q23]), "radius" : 2.5 * mm, "tangentPropagation" : true, "allowEdgeOverflow" : false});
        }
        {
            var Q0;
            Q0=makeQuery(id+"F1.opExtrude","CAP_FACE",FACE,{"disambiguationData":[OSD([sQuery(id+"F0.wireOp",EDGE,"E0.bottom"),sQuery(id+"F0.wireOp",EDGE,"E0.top"),sQuery(id+"F0.wireOp",EDGE,"E1"),sQuery(id+"F0.wireOp",EDGE,"E2")])],"isStart":false});
            var sketch = newSketch(context, id + "F15", { "sketchPlane" : qUnion([Q0])});
            skLineSegment(sketch, "E47.top", {"start": v(-280, -75) * mm, "end": v(-180, -75) * mm});
            skLineSegment(sketch, "E47.left", {"start": v(-280, 75) * mm, "end": v(-280, -75) * mm});
            skLineSegment(sketch, "E47.right", {"start": v(-180, 75) * mm, "end": v(-180, -75) * mm});
            skPoint(sketch, "E47.middle", {"position": v(-230, 0) * mm});
            skLineSegment(sketch, "E48.bottom", {"start": v(180, -75) * mm, "end": v(280, -75) * mm});
            skLineSegment(sketch, "E48.top", {"start": v(180, 75) * mm, "end": v(280, 75) * mm});
            skLineSegment(sketch, "E48.left", {"start": v(180, -75) * mm, "end": v(180, 75) * mm});
            skLineSegment(sketch, "E48.right", {"start": v(280, -75) * mm, "end": v(280, 75) * mm});
            skPoint(sketch, "E48.middle", {"position": v(230, 0) * mm});
            skLineSegment(sketch, "E49", {"start": v(-180, 75) * mm, "end": v(-280, 75) * mm});
            skLineSegment(sketch, "E50", {"start": v(180, 70) * mm, "end": v(280, 70) * mm});
            skLineSegment(sketch, "E51.0.1.0", {"start": v(-280, 65) * mm, "end": v(-180, 65) * mm});
            skLineSegment(sketch, "E51.0.1.1", {"start": v(-180, 70) * mm, "end": v(-280, 70) * mm});
            skLineSegment(sketch, "E51.0.2.0", {"start": v(180, 60) * mm, "end": v(280, 60) * mm});
            skLineSegment(sketch, "E51.0.2.1", {"start": v(280, 65) * mm, "end": v(180, 65) * mm});
            skLineSegment(sketch, "E51.0.3.0", {"start": v(-280, 55) * mm, "end": v(-180, 55) * mm});
            skLineSegment(sketch, "E51.0.3.1", {"start": v(-180, 60) * mm, "end": v(-280, 60) * mm});
            skLineSegment(sketch, "E51.0.4.0", {"start": v(-280, 50) * mm, "end": v(-180, 50) * mm});
            skLineSegment(sketch, "E51.0.4.1", {"start": v(280, 55) * mm, "end": v(180, 55) * mm});
            skLineSegment(sketch, "E51.0.5.0", {"start": v(180, 45) * mm, "end": v(280, 45) * mm});
            skLineSegment(sketch, "E51.0.5.1", {"start": v(280, 50) * mm, "end": v(180, 50) * mm});
            skLineSegment(sketch, "E51.0.6.0", {"start": v(-280, 40) * mm, "end": v(-180, 40) * mm});
            skLineSegment(sketch, "E51.0.6.1", {"start": v(-180, 45) * mm, "end": v(-280, 45) * mm});
            skLineSegment(sketch, "E51.0.7.0", {"start": v(-280, 35) * mm, "end": v(-180, 35) * mm});
            skLineSegment(sketch, "E51.0.7.1", {"start": v(280, 40) * mm, "end": v(180, 40) * mm});
            skLineSegment(sketch, "E51.0.8.0", {"start": v(180, 30) * mm, "end": v(280, 30) * mm});
            skLineSegment(sketch, "E51.0.8.1", {"start": v(280, 35) * mm, "end": v(180, 35) * mm});
            skLineSegment(sketch, "E51.0.9.0", {"start": v(-280, 25) * mm, "end": v(-180, 25) * mm});
            skLineSegment(sketch, "E51.0.9.1", {"start": v(-180, 30) * mm, "end": v(-280, 30) * mm});
            skLineSegment(sketch, "E51.0.10.0", {"start": v(-280, 20) * mm, "end": v(-180, 20) * mm});
            skLineSegment(sketch, "E51.0.10.1", {"start": v(280, 25) * mm, "end": v(180, 25) * mm});
            skLineSegment(sketch, "E51.0.11.0", {"start": v(-280, 15) * mm, "end": v(-180, 15) * mm});
            skLineSegment(sketch, "E51.0.11.1", {"start": v(280, 20) * mm, "end": v(180, 20) * mm});
            skLineSegment(sketch, "E51.0.12.0", {"start": v(-280, 10) * mm, "end": v(-180, 10) * mm});
            skLineSegment(sketch, "E51.0.12.1", {"start": v(280, 15) * mm, "end": v(180, 15) * mm});
            skLineSegment(sketch, "E51.0.13.0", {"start": v(180, 5) * mm, "end": v(280, 5) * mm});
            skLineSegment(sketch, "E51.0.13.1", {"start": v(280, 10) * mm, "end": v(180, 10) * mm});
            skLineSegment(sketch, "E51.0.14.0", {"start": v(-280, 0) * mm, "end": v(-180, 0) * mm});
            skLineSegment(sketch, "E51.0.14.1", {"start": v(-180, 5) * mm, "end": v(-280, 5) * mm});
            skLineSegment(sketch, "E51.0.15.0", {"start": v(-280, -5) * mm, "end": v(-180, -5) * mm});
            skLineSegment(sketch, "E51.0.15.1", {"start": v(280, 0) * mm, "end": v(180, 0) * mm});
            skLineSegment(sketch, "E51.0.16.0", {"start": v(180, -10) * mm, "end": v(280, -10) * mm});
            skLineSegment(sketch, "E51.0.16.1", {"start": v(280, -5) * mm, "end": v(180, -5) * mm});
            skLineSegment(sketch, "E51.0.17.0", {"start": v(-280, -15) * mm, "end": v(-180, -15) * mm});
            skLineSegment(sketch, "E51.0.17.1", {"start": v(-180, -10) * mm, "end": v(-280, -10) * mm});
            skLineSegment(sketch, "E51.0.18.0", {"start": v(-280, -20) * mm, "end": v(-180, -20) * mm});
            skLineSegment(sketch, "E51.0.18.1", {"start": v(280, -15) * mm, "end": v(180, -15) * mm});
            skLineSegment(sketch, "E51.0.19.0", {"start": v(-280, -25) * mm, "end": v(-180, -25) * mm});
            skLineSegment(sketch, "E51.0.19.1", {"start": v(280, -20) * mm, "end": v(180, -20) * mm});
            skLineSegment(sketch, "E51.0.20.0", {"start": v(-280, -30) * mm, "end": v(-180, -30) * mm});
            skLineSegment(sketch, "E51.0.20.1", {"start": v(280, -25) * mm, "end": v(180, -25) * mm});
            skLineSegment(sketch, "E51.0.21.0", {"start": v(180, -35) * mm, "end": v(280, -35) * mm});
            skLineSegment(sketch, "E51.0.21.1", {"start": v(280, -30) * mm, "end": v(180, -30) * mm});
            skLineSegment(sketch, "E51.0.22.0", {"start": v(-280, -40) * mm, "end": v(-180, -40) * mm});
            skLineSegment(sketch, "E51.0.22.1", {"start": v(-180, -35) * mm, "end": v(-280, -35) * mm});
            skLineSegment(sketch, "E51.0.23.0", {"start": v(-280, -45) * mm, "end": v(-180, -45) * mm});
            skLineSegment(sketch, "E51.0.23.1", {"start": v(280, -40) * mm, "end": v(180, -40) * mm});
            skLineSegment(sketch, "E51.0.24.0", {"start": v(180, -50) * mm, "end": v(280, -50) * mm});
            skLineSegment(sketch, "E51.0.24.1", {"start": v(280, -45) * mm, "end": v(180, -45) * mm});
            skLineSegment(sketch, "E51.0.25.0", {"start": v(-280, -55) * mm, "end": v(-180, -55) * mm});
            skLineSegment(sketch, "E51.0.25.1", {"start": v(-180, -50) * mm, "end": v(-280, -50) * mm});
            skLineSegment(sketch, "E51.0.26.0", {"start": v(-280, -60) * mm, "end": v(-180, -60) * mm});
            skLineSegment(sketch, "E51.0.26.1", {"start": v(280, -55) * mm, "end": v(180, -55) * mm});
            skLineSegment(sketch, "E51.0.27.0", {"start": v(-280, -65) * mm, "end": v(-180, -65) * mm});
            skLineSegment(sketch, "E51.0.27.1", {"start": v(280, -60) * mm, "end": v(180, -60) * mm});
            skLineSegment(sketch, "E51.0.28.0", {"start": v(-280, -70) * mm, "end": v(-180, -70) * mm});
            skLineSegment(sketch, "E51.0.28.1", {"start": v(280, -65) * mm, "end": v(180, -65) * mm});
            skLineSegment(sketch, "E51.0.29.1", {"start": v(280, -70) * mm, "end": v(180, -70) * mm});
            skLineSegment(sketch, "E51.direction2", {"start": v(-280, 70) * mm, "end": v(-280, 65) * mm, "construction": true});
            skSolve(sketch);
        }
        {
            var Q0;
            {var subQ0=sQuery(id+"F15.wireOp",EDGE,"E49");Q0=makeQuery(id+"F15.imprint","IMPRINT",FACE,{"disambiguationData":[TD([[makeQuery(id+"F15.imprint","IMPRINT",EDGE,{"derivedFrom":subQ0}),1.0]])]});}
            var Q1;
            {var subQ0=sQuery(id+"F15.wireOp",EDGE,"E51.0.1.0");Q1=makeQuery(id+"F15.imprint","IMPRINT",FACE,{"disambiguationData":[TD([[makeQuery(id+"F15.imprint","IMPRINT",EDGE,{"derivedFrom":subQ0}),-1.0]])]});}
            var Q2;
            {var subQ0=sQuery(id+"F15.wireOp",EDGE,"E51.0.3.0");Q2=makeQuery(id+"F15.imprint","IMPRINT",FACE,{"disambiguationData":[TD([[makeQuery(id+"F15.imprint","IMPRINT",EDGE,{"derivedFrom":subQ0}),-1.0]])]});}
            var Q3;
            {var subQ0=sQuery(id+"F15.wireOp",EDGE,"E51.0.6.0");Q3=makeQuery(id+"F15.imprint","IMPRINT",FACE,{"disambiguationData":[TD([[makeQuery(id+"F15.imprint","IMPRINT",EDGE,{"derivedFrom":subQ0}),1.0]])]});}
            var Q4;
            {var subQ0=sQuery(id+"F15.wireOp",EDGE,"E51.0.7.0");Q4=makeQuery(id+"F15.imprint","IMPRINT",FACE,{"disambiguationData":[TD([[makeQuery(id+"F15.imprint","IMPRINT",EDGE,{"derivedFrom":subQ0}),-1.0]])]});}
            var Q5;
            {var subQ0=sQuery(id+"F15.wireOp",EDGE,"E51.0.9.0");Q5=makeQuery(id+"F15.imprint","IMPRINT",FACE,{"disambiguationData":[TD([[makeQuery(id+"F15.imprint","IMPRINT",EDGE,{"derivedFrom":subQ0}),-1.0]])]});}
            var Q6;
            {var subQ0=sQuery(id+"F15.wireOp",EDGE,"E51.0.11.0");Q6=makeQuery(id+"F15.imprint","IMPRINT",FACE,{"disambiguationData":[TD([[makeQuery(id+"F15.imprint","IMPRINT",EDGE,{"derivedFrom":subQ0}),-1.0]])]});}
            var Q7;
            {var subQ0=sQuery(id+"F15.wireOp",EDGE,"E51.0.14.0");Q7=makeQuery(id+"F15.imprint","IMPRINT",FACE,{"disambiguationData":[TD([[makeQuery(id+"F15.imprint","IMPRINT",EDGE,{"derivedFrom":subQ0}),1.0]])]});}
            var Q8;
            {var subQ0=sQuery(id+"F15.wireOp",EDGE,"E51.0.15.0");Q8=makeQuery(id+"F15.imprint","IMPRINT",FACE,{"disambiguationData":[TD([[makeQuery(id+"F15.imprint","IMPRINT",EDGE,{"derivedFrom":subQ0}),-1.0]])]});}
            var Q9;
            {var subQ0=sQuery(id+"F15.wireOp",EDGE,"E51.0.17.0");Q9=makeQuery(id+"F15.imprint","IMPRINT",FACE,{"disambiguationData":[TD([[makeQuery(id+"F15.imprint","IMPRINT",EDGE,{"derivedFrom":subQ0}),-1.0]])]});}
            var Q10;
            {var subQ0=sQuery(id+"F15.wireOp",EDGE,"E51.0.19.0");Q10=makeQuery(id+"F15.imprint","IMPRINT",FACE,{"disambiguationData":[TD([[makeQuery(id+"F15.imprint","IMPRINT",EDGE,{"derivedFrom":subQ0}),-1.0]])]});}
            var Q11;
            {var subQ0=sQuery(id+"F15.wireOp",EDGE,"E51.0.22.0");Q11=makeQuery(id+"F15.imprint","IMPRINT",FACE,{"disambiguationData":[TD([[makeQuery(id+"F15.imprint","IMPRINT",EDGE,{"derivedFrom":subQ0}),1.0]])]});}
            var Q12;
            {var subQ0=sQuery(id+"F15.wireOp",EDGE,"E51.0.23.0");Q12=makeQuery(id+"F15.imprint","IMPRINT",FACE,{"disambiguationData":[TD([[makeQuery(id+"F15.imprint","IMPRINT",EDGE,{"derivedFrom":subQ0}),-1.0]])]});}
            var Q13;
            {var subQ0=sQuery(id+"F15.wireOp",EDGE,"E51.0.25.0");Q13=makeQuery(id+"F15.imprint","IMPRINT",FACE,{"disambiguationData":[TD([[makeQuery(id+"F15.imprint","IMPRINT",EDGE,{"derivedFrom":subQ0}),-1.0]])]});}
            var Q14;
            {var subQ0=sQuery(id+"F15.wireOp",EDGE,"E51.0.27.0");Q14=makeQuery(id+"F15.imprint","IMPRINT",FACE,{"disambiguationData":[TD([[makeQuery(id+"F15.imprint","IMPRINT",EDGE,{"derivedFrom":subQ0}),-1.0]])]});}
            var Q15;
            {var subQ0=sQuery(id+"F15.wireOp",EDGE,"E48.top");Q15=makeQuery(id+"F15.imprint","IMPRINT",FACE,{"disambiguationData":[TD([[makeQuery(id+"F15.imprint","IMPRINT",EDGE,{"derivedFrom":subQ0}),-1.0]])]});}
            var Q16;
            {var subQ0=sQuery(id+"F15.wireOp",EDGE,"E51.0.2.0");Q16=makeQuery(id+"F15.imprint","IMPRINT",FACE,{"disambiguationData":[TD([[makeQuery(id+"F15.imprint","IMPRINT",EDGE,{"derivedFrom":subQ0}),1.0]])]});}
            var Q17;
            {var subQ0=sQuery(id+"F15.wireOp",EDGE,"E51.0.4.1");Q17=makeQuery(id+"F15.imprint","IMPRINT",FACE,{"disambiguationData":[TD([[makeQuery(id+"F15.imprint","IMPRINT",EDGE,{"derivedFrom":subQ0}),1.0]])]});}
            var Q18;
            {var subQ0=sQuery(id+"F15.wireOp",EDGE,"E51.0.5.0");Q18=makeQuery(id+"F15.imprint","IMPRINT",FACE,{"disambiguationData":[TD([[makeQuery(id+"F15.imprint","IMPRINT",EDGE,{"derivedFrom":subQ0}),-1.0]])]});}
            var Q19;
            {var subQ0=sQuery(id+"F15.wireOp",EDGE,"E51.0.8.0");Q19=makeQuery(id+"F15.imprint","IMPRINT",FACE,{"disambiguationData":[TD([[makeQuery(id+"F15.imprint","IMPRINT",EDGE,{"derivedFrom":subQ0}),1.0]])]});}
            var Q20;
            {var subQ0=sQuery(id+"F15.wireOp",EDGE,"E51.0.10.1");Q20=makeQuery(id+"F15.imprint","IMPRINT",FACE,{"disambiguationData":[TD([[makeQuery(id+"F15.imprint","IMPRINT",EDGE,{"derivedFrom":subQ0}),1.0]])]});}
            var Q21;
            {var subQ0=sQuery(id+"F15.wireOp",EDGE,"E51.0.12.1");Q21=makeQuery(id+"F15.imprint","IMPRINT",FACE,{"disambiguationData":[TD([[makeQuery(id+"F15.imprint","IMPRINT",EDGE,{"derivedFrom":subQ0}),1.0]])]});}
            var Q22;
            {var subQ0=sQuery(id+"F15.wireOp",EDGE,"E51.0.13.0");Q22=makeQuery(id+"F15.imprint","IMPRINT",FACE,{"disambiguationData":[TD([[makeQuery(id+"F15.imprint","IMPRINT",EDGE,{"derivedFrom":subQ0}),-1.0]])]});}
            var Q23;
            {var subQ0=sQuery(id+"F15.wireOp",EDGE,"E51.0.16.0");Q23=makeQuery(id+"F15.imprint","IMPRINT",FACE,{"disambiguationData":[TD([[makeQuery(id+"F15.imprint","IMPRINT",EDGE,{"derivedFrom":subQ0}),1.0]])]});}
            var Q24;
            {var subQ0=sQuery(id+"F15.wireOp",EDGE,"E51.0.18.1");Q24=makeQuery(id+"F15.imprint","IMPRINT",FACE,{"disambiguationData":[TD([[makeQuery(id+"F15.imprint","IMPRINT",EDGE,{"derivedFrom":subQ0}),1.0]])]});}
            var Q25;
            {var subQ0=sQuery(id+"F15.wireOp",EDGE,"E51.0.20.1");Q25=makeQuery(id+"F15.imprint","IMPRINT",FACE,{"disambiguationData":[TD([[makeQuery(id+"F15.imprint","IMPRINT",EDGE,{"derivedFrom":subQ0}),1.0]])]});}
            var Q26;
            {var subQ0=sQuery(id+"F15.wireOp",EDGE,"E51.0.21.0");Q26=makeQuery(id+"F15.imprint","IMPRINT",FACE,{"disambiguationData":[TD([[makeQuery(id+"F15.imprint","IMPRINT",EDGE,{"derivedFrom":subQ0}),-1.0]])]});}
            var Q27;
            {var subQ0=sQuery(id+"F15.wireOp",EDGE,"E51.0.24.0");Q27=makeQuery(id+"F15.imprint","IMPRINT",FACE,{"disambiguationData":[TD([[makeQuery(id+"F15.imprint","IMPRINT",EDGE,{"derivedFrom":subQ0}),1.0]])]});}
            var Q28;
            {var subQ0=sQuery(id+"F15.wireOp",EDGE,"E51.0.26.1");Q28=makeQuery(id+"F15.imprint","IMPRINT",FACE,{"disambiguationData":[TD([[makeQuery(id+"F15.imprint","IMPRINT",EDGE,{"derivedFrom":subQ0}),1.0]])]});}
            var Q29;
            {var subQ0=sQuery(id+"F15.wireOp",EDGE,"E51.0.28.1");Q29=makeQuery(id+"F15.imprint","IMPRINT",FACE,{"disambiguationData":[TD([[makeQuery(id+"F15.imprint","IMPRINT",EDGE,{"derivedFrom":subQ0}),1.0]])]});}
            extrude(context, id + "F16", {"entities" : qUnion([Q0, Q1, Q2, Q3, Q4, Q5, Q6, Q7, Q8, Q9, Q10, Q11, Q12, Q13, Q14, Q15, Q16, Q17, Q18, Q19, Q20, Q21, Q22, Q23, Q24, Q25, Q26, Q27, Q28, Q29]), "operationType" : NewBodyOperationType.ADD, "depth" : 1 * mm, "offsetDistance" : 25 * mm});
        }
        {
            var Q0;
            Q0=makeQuery(id+"F1.opExtrude","CAP_FACE",FACE,{"disambiguationData":[OSD([sQuery(id+"F0.wireOp",EDGE,"E0.bottom"),sQuery(id+"F0.wireOp",EDGE,"E0.top"),sQuery(id+"F0.wireOp",EDGE,"E1"),sQuery(id+"F0.wireOp",EDGE,"E2")])],"isStart":false});
            var sketch = newSketch(context, id + "F17", { "sketchPlane" : qUnion([Q0])});
            skEllipse(sketch, "E52", {"center": v(0, -101.34) * mm, "majorRadius": 35 * mm, "minorRadius": 15 * mm, "majorAxis": v(-1, 0)});
            skSolve(sketch);
        }
        {
            var Q0;
            Q0=makeQuery(id+"F17.imprint","IMPRINT",FACE,{"disambiguationData":[TD([[makeQuery(id+"F17.imprint","IMPRINT",EDGE,{"derivedFrom":sQuery(id+"F17.wireOp",EDGE,"E52")}),1.0]])]});
            extrude(context, id + "F18", {"entities" : qUnion([Q0]), "operationType" : NewBodyOperationType.ADD, "depth" : 30 * mm, "offsetDistance" : 25 * mm});
        }
        {
            var Q0;
            Q0=makeQuery(id+"F18.opExtrude","CAP_EDGE",EDGE,{"disambiguationData":[OSD([sQuery(id+"F17.wireOp",EDGE,"E52")])],"isStart":false});
            fillet(context, id + "F19", {"entities" : qUnion([Q0]), "radius" : 10 * mm, "tangentPropagation" : true, "allowEdgeOverflow" : false});
        }
        {
            var Q0;
            Q0=makeQuery(id+"F18.opExtrude","CAP_FACE",FACE,{"disambiguationData":[OSD([sQuery(id+"F17.wireOp",EDGE,"E52")])],"isStart":false});
            extrude(context, id + "F20", {"entities" : qUnion([Q0]), "operationType" : NewBodyOperationType.ADD, "depth" : 2 * mm, "offsetDistance" : 25 * mm});
        }
        {
            var Q0;
            {var subQ0=sQuery(id+"F17.wireOp",EDGE,"E52");Q0=makeQuery(id+"F20.opExtrude","CAP_EDGE",EDGE,{"disambiguationData":[OSD([subQ0]),TDD([makeQuery(id+"F19.opFillet","BLEND_EDGE",EDGE,{"disambiguationData":[OD(1.0)],"blendedFrom":[makeQuery(id+"F18.opExtrude","CAP_EDGE",EDGE,{"disambiguationData":[OSD([subQ0])],"isStart":false}),makeQuery(id+"F18.opExtrude","CAP_FACE",FACE,{"disambiguationData":[OSD([subQ0])],"isStart":false})],"blendedInto":[makeQuery(id+"F18.opExtrude","CAP_FACE",FACE,{"disambiguationData":[OSD([subQ0])],"isStart":false})]})])],"isStart":false});}
            var Q1;
            {var subQ0=sQuery(id+"F17.wireOp",EDGE,"E52");Q1=makeQuery(id+"F20.opExtrude","CAP_EDGE",EDGE,{"disambiguationData":[OSD([subQ0]),TDD([makeQuery(id+"F19.opFillet","BLEND_EDGE",EDGE,{"disambiguationData":[OD(0.0)],"blendedFrom":[makeQuery(id+"F18.opExtrude","CAP_EDGE",EDGE,{"disambiguationData":[OSD([subQ0])],"isStart":false}),makeQuery(id+"F18.opExtrude","CAP_FACE",FACE,{"disambiguationData":[OSD([subQ0])],"isStart":false})],"blendedInto":[makeQuery(id+"F18.opExtrude","CAP_FACE",FACE,{"disambiguationData":[OSD([subQ0])],"isStart":false})]})])],"isStart":false});}
            fillet(context, id + "F21", {"entities" : qUnion([Q0, Q1]), "radius" : 5 * mm, "tangentPropagation" : true, "allowEdgeOverflow" : false});
        }
        {
            var Q0;
            Q0=makeQuery(id+"F1.opExtrude","CAP_FACE",FACE,{"disambiguationData":[OSD([sQuery(id+"F0.wireOp",EDGE,"E0.bottom"),sQuery(id+"F0.wireOp",EDGE,"E0.top"),sQuery(id+"F0.wireOp",EDGE,"E1"),sQuery(id+"F0.wireOp",EDGE,"E2")])],"isStart":false});
            var sketch = newSketch(context, id + "F22", { "sketchPlane" : qUnion([Q0])});
            skLineSegment(sketch, "E53.bottom", {"start": v(-257.58, 132.38) * mm, "end": v(-224.28, 132.38) * mm});
            skLineSegment(sketch, "E53.top", {"start": v(-257.58, 103.15) * mm, "end": v(-224.28, 103.15) * mm});
            skLineSegment(sketch, "E53.left", {"start": v(-257.58, 132.38) * mm, "end": v(-257.58, 103.15) * mm});
            skLineSegment(sketch, "E53.right", {"start": v(-224.28, 132.38) * mm, "end": v(-224.28, 103.15) * mm});
            skLineSegment(sketch, "E54.bottom", {"start": v(-224.28, 110.92) * mm, "end": v(-223.16, 110.92) * mm});
            skLineSegment(sketch, "E54.top", {"start": v(-224.28, 124.62) * mm, "end": v(-223.16, 124.62) * mm});
            skLineSegment(sketch, "E54.left", {"start": v(-224.28, 110.92) * mm, "end": v(-224.28, 124.62) * mm});
            skLineSegment(sketch, "E54.right", {"start": v(-223.16, 110.92) * mm, "end": v(-223.16, 124.62) * mm});
            skPoint(sketch, "E54.middle", {"position": v(-223.72, 117.77) * mm});
            skPoint(sketch, "E54.middle.positionSnap0", {"position": v(-224.28, 117.77) * mm});
            skPoint(sketch, "E54.centerSnap0", {"position": v(-224.28, 117.77) * mm});
            skLineSegment(sketch, "E55.bottom", {"start": v(-220.7, 110.92) * mm, "end": v(-223.16, 110.92) * mm});
            skLineSegment(sketch, "E55.top", {"start": v(-220.7, 124.62) * mm, "end": v(-223.16, 124.62) * mm});
            skLineSegment(sketch, "E55.left", {"start": v(-220.7, 110.92) * mm, "end": v(-220.7, 124.62) * mm});
            skPoint(sketch, "E55.middle", {"position": v(-221.93, 117.77) * mm});
            skPoint(sketch, "E55.middle.positionSnap0", {"position": v(-223.16, 117.77) * mm});
            skPoint(sketch, "E55.centerSnap0", {"position": v(-223.16, 117.77) * mm});
            skPoint(sketch, "E56.startSnap0", {"position": v(-240.93, 132.38) * mm});
            skPoint(sketch, "E56.startSnap1", {"position": v(-257.58, 117.77) * mm});
            skPoint(sketch, "E57.endSnap0", {"position": v(-240.93, 103.15) * mm});
            skLineSegment(sketch, "E58", {"start": v(-237.39, 110.92) * mm, "end": v(-245.91, 104.59) * mm});
            skLineSegment(sketch, "E59", {"start": v(-234.02, 130.16) * mm, "end": v(-238.82, 121.02) * mm});
            skPoint(sketch, "E60.endSnap0", {"position": v(-239.44, 110.92) * mm});
            skLineSegment(sketch, "E61", {"start": v(-234.7, 120.17) * mm, "end": v(-238.82, 121.02) * mm});
            skLineSegment(sketch, "E62", {"start": v(-234.02, 130.16) * mm, "end": v(-240.38, 130.16) * mm});
            skLineSegment(sketch, "E63", {"start": v(-240.38, 130.16) * mm, "end": v(-246.58, 118.34) * mm});
            skLineSegment(sketch, "E64", {"start": v(-240.83, 118.24) * mm, "end": v(-246.58, 118.34) * mm});
            skLineSegment(sketch, "E65", {"start": v(-234.7, 120.17) * mm, "end": v(-239.56, 114.34) * mm});
            skLineSegment(sketch, "E66", {"start": v(-239.56, 114.34) * mm, "end": v(-237.39, 110.92) * mm});
            skLineSegment(sketch, "E67", {"start": v(-245.91, 104.59) * mm, "end": v(-241.65, 111.26) * mm});
            skPoint(sketch, "E67.endSnap0", {"position": v(-241.65, 107.76) * mm});
            skLineSegment(sketch, "E68", {"start": v(-241.65, 111.26) * mm, "end": v(-243.36, 114.5) * mm});
            skLineSegment(sketch, "E69", {"start": v(-243.36, 114.5) * mm, "end": v(-240.83, 118.24) * mm});
            skSolve(sketch);
        }
        {
            var Q0;
            Q0=makeQuery(id+"F22.imprint","IMPRINT",FACE,{"disambiguationData":[TD([[makeQuery(id+"F22.imprint","IMPRINT",EDGE,{"derivedFrom":sQuery(id+"F22.wireOp",EDGE,"E54.bottom")}),1.0]])]});
            extrude(context, id + "F23", {"entities" : qUnion([Q0]), "operationType" : NewBodyOperationType.REMOVE, "oppositeDirection" : true, "depth" : 1 * mm, "offsetDistance" : 25 * mm});
        }
        {
            var Q0;
            {var subQ1=sQuery(id+"F22.wireOp",EDGE,"E53.bottom");Q0=makeQuery(id+"F22.imprint","IMPRINT",FACE,{"disambiguationData":[TD([[makeQuery(id+"F22.imprint","IMPRINT",EDGE,{"derivedFrom":subQ1}),-1.0]])]});}
            var Q1;
            {var subQ0=sQuery(id+"F22.wireOp",EDGE,"E54.right");Q1=makeQuery(id+"F22.imprint","IMPRINT",FACE,{"disambiguationData":[TD([[makeQuery(id+"F22.imprint","IMPRINT",EDGE,{"derivedFrom":subQ0}),-1.0]])]});}
            extrude(context, id + "F24", {"entities" : qUnion([Q0, Q1]), "operationType" : NewBodyOperationType.ADD, "depth" : 1 * mm, "offsetDistance" : 25 * mm});
        }
        {
            var Q0;
            Q0=makeQuery(id+"F22.imprint","IMPRINT",FACE,{"disambiguationData":[TD([[makeQuery(id+"F22.imprint","IMPRINT",EDGE,{"derivedFrom":sQuery(id+"F22.wireOp",EDGE,"E58")}),-1.0]])]});
            extrude(context, id + "F25", {"entities" : qUnion([Q0]), "operationType" : NewBodyOperationType.ADD, "depth" : 2.5 * mm, "offsetDistance" : 25 * mm});
        }
    });
